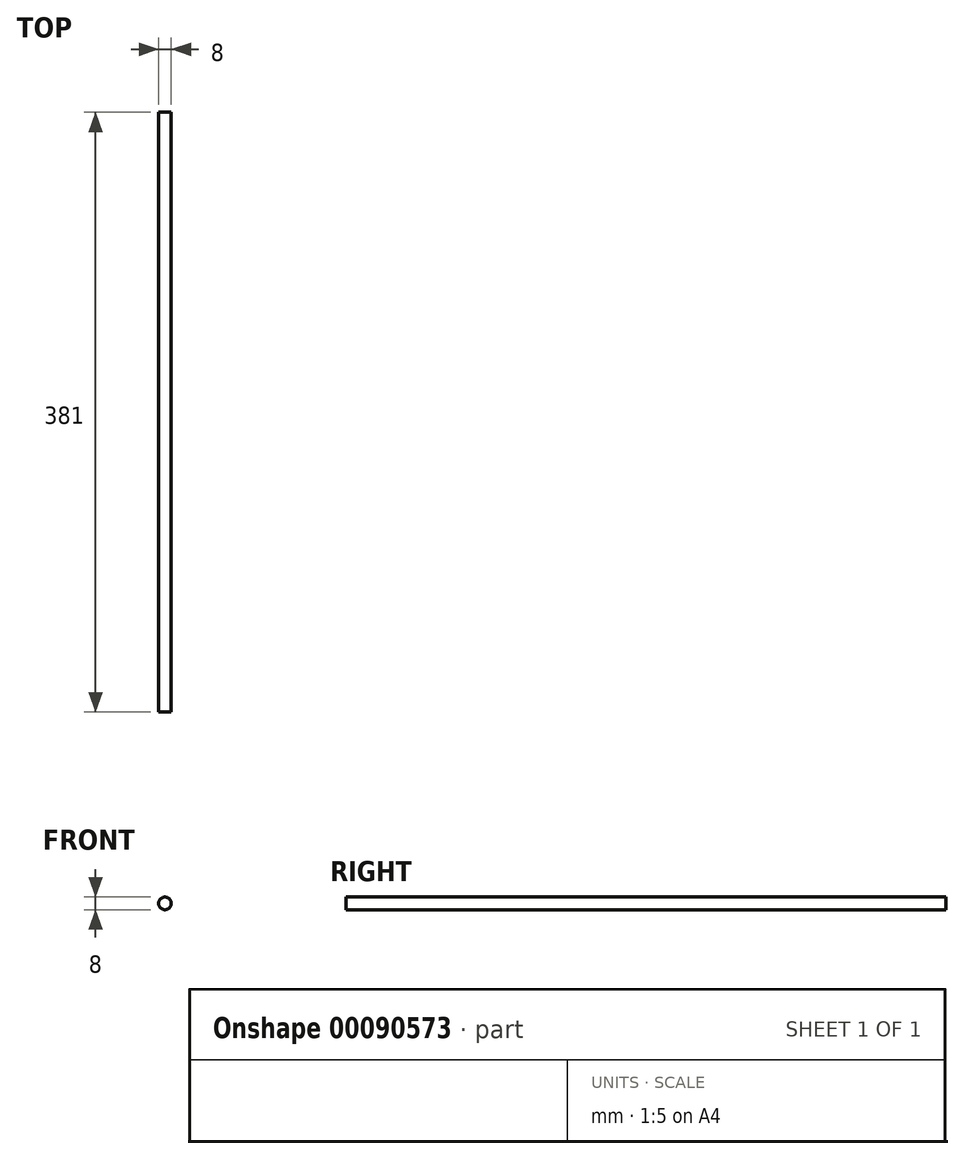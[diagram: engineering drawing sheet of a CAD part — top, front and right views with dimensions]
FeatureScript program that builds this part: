
annotation { "Feature Type Name" : "Feature", "Feature Type Description" : "" }
export const myFeature = defineFeature(function(context is Context, id is Id, definition is map)
    precondition{}
    {
        {
            var Q0;
            Q0=qCreatedBy(makeId("Front.planeOp"),FACE);
            var sketch = newSketch(context, id + "F0", { "sketchPlane" : qUnion([Q0])});
            skCircle(sketch, "E0", {"center": v(0, 0) * mm, "radius": 4 * mm});
            skSolve(sketch);
        }
        {
            var Q0;
            Q0=makeQuery(id+"F0.imprint","IMPRINT",FACE,{"disambiguationData":[TD([[makeQuery(id+"F0.imprint","IMPRINT",EDGE,{"derivedFrom":sQuery(id+"F0.wireOp",EDGE,"E0")}),1.0]])]});
            extrude(context, id + "F1", {"entities" : qUnion([Q0]), "depth" : 381 * mm});
        }
    });
